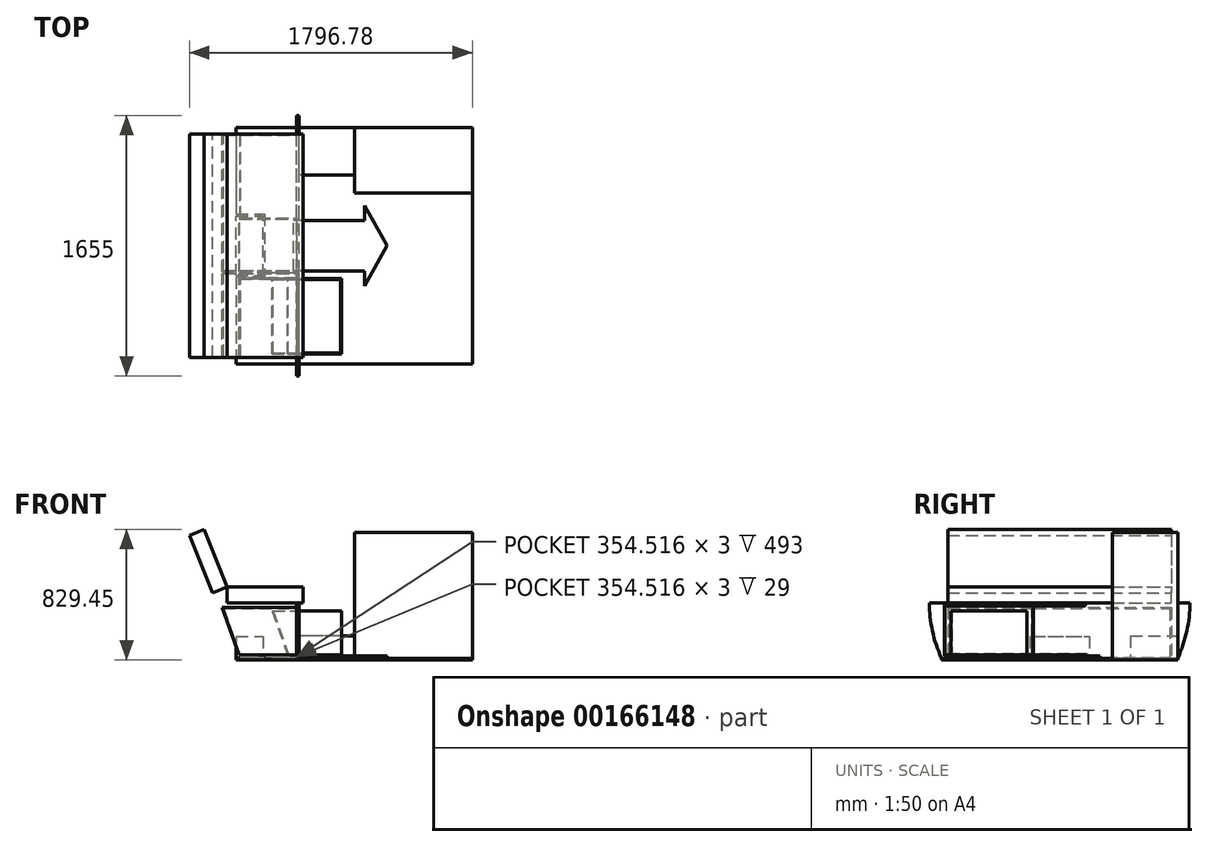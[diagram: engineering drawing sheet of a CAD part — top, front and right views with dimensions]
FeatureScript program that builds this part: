
annotation { "Feature Type Name" : "Feature", "Feature Type Description" : "" }
export const myFeature = defineFeature(function(context is Context, id is Id, definition is map)
    precondition{}
    {
        {
            var Q0;
            Q0=qCreatedBy(makeId("Top.planeOp"),FACE);
            var sketch = newSketch(context, id + "F0", { "sketchPlane" : qUnion([Q0])});
            skLineSegment(sketch, "E0.bottom", {"start": v(750, 750) * mm, "end": v(-750, 750) * mm});
            skLineSegment(sketch, "E0.top", {"start": v(750, -750) * mm, "end": v(-750, -750) * mm});
            skLineSegment(sketch, "E0.left", {"start": v(750, 750) * mm, "end": v(750, -750) * mm});
            skLineSegment(sketch, "E0.right", {"start": v(-750, 750) * mm, "end": v(-750, 200) * mm});
            skPoint(sketch, "E0.middle", {"position": v(0, 0) * mm});
            skLineSegment(sketch, "E1", {"start": v(-750, 200) * mm, "end": v(-570, 200) * mm});
            skLineSegment(sketch, "E2", {"start": v(-570, 200) * mm, "end": v(-570, -200) * mm});
            skLineSegment(sketch, "E3", {"start": v(-570, -200) * mm, "end": v(-750, -200) * mm});
            skLineSegment(sketch, "E4.trimOffspring", {"start": v(-750, -200) * mm, "end": v(-750, -750) * mm});
            skLineSegment(sketch, "E5", {"start": v(-750, 0) * mm, "end": v(750, 0) * mm, "construction": true});
            skSolve(sketch);
        }
        {
            var Q0;
            Q0=makeQuery(id+"F0.imprint","IMPRINT",FACE,{"disambiguationData":[TD([[makeQuery(id+"F0.imprint","IMPRINT",EDGE,{"derivedFrom":sQuery(id+"F0.wireOp",EDGE,"E0.bottom")}),1.0]])]});
            extrude(context, id + "F1", {"entities" : qUnion([Q0]), "depth" : 12 * mm});
        }
        {
            var Q0;
            Q0=makeQuery(id+"F1.opExtrude","CAP_FACE",FACE,{"disambiguationData":[OSD([sQuery(id+"F0.wireOp",EDGE,"E0.bottom"),sQuery(id+"F0.wireOp",EDGE,"E0.top"),sQuery(id+"F0.wireOp",EDGE,"E0.left"),sQuery(id+"F0.wireOp",EDGE,"E0.right"),sQuery(id+"F0.wireOp",EDGE,"E1"),sQuery(id+"F0.wireOp",EDGE,"E2"),sQuery(id+"F0.wireOp",EDGE,"E3"),sQuery(id+"F0.wireOp",EDGE,"E4.trimOffspring")])],"isStart":false});
            var sketch = newSketch(context, id + "F2", { "sketchPlane" : qUnion([Q0])});
            skLineSegment(sketch, "E6", {"start": v(-350, 750) * mm, "end": v(-350, -750) * mm, "construction": true});
            skLineSegment(sketch, "E7", {"start": v(0, 750) * mm, "end": v(0, 335) * mm, "construction": true});
            skLineSegment(sketch, "E8", {"start": v(0, 335) * mm, "end": v(750, 335) * mm, "construction": true});
            skLineSegment(sketch, "E9", {"start": v(-350, 450) * mm, "end": v(0, 450) * mm, "construction": true});
            skLineSegment(sketch, "E10", {"start": v(-366, 750) * mm, "end": v(-366, -750) * mm});
            skLineSegment(sketch, "E11", {"start": v(16, 466) * mm, "end": v(-366, 466) * mm});
            skLineSegment(sketch, "E12", {"start": v(16, 466) * mm, "end": v(16, 351) * mm});
            skLineSegment(sketch, "E13", {"start": v(750, 351) * mm, "end": v(16, 351) * mm});
            skLineSegment(sketch, "E14", {"start": v(-350, -750) * mm, "end": v(-350, -770) * mm});
            skLineSegment(sketch, "E15", {"start": v(-350, -770) * mm, "end": v(750, -770) * mm});
            skLineSegment(sketch, "E16", {"start": v(750, -770) * mm, "end": v(750, -750) * mm});
            skLineSegment(sketch, "E17.bottom", {"start": v(-350, -705) * mm, "end": v(750, -705) * mm});
            skLineSegment(sketch, "E17.top", {"start": v(-350, -670) * mm, "end": v(750, -670) * mm});
            skLineSegment(sketch, "E17.left", {"start": v(-350, -705) * mm, "end": v(-350, -670) * mm});
            skLineSegment(sketch, "E17.right", {"start": v(750, -705) * mm, "end": v(750, -670) * mm});
            skLineSegment(sketch, "E18", {"start": v(-350, -710) * mm, "end": v(750, -710) * mm});
            skLineSegment(sketch, "E19", {"start": v(750, -710) * mm, "end": v(750, -750) * mm});
            skLineSegment(sketch, "E20", {"start": v(-350, -710) * mm, "end": v(-350, -750) * mm});
            skLineSegment(sketch, "E21.bottom", {"start": v(-350, 450) * mm, "end": v(0, 450) * mm});
            skLineSegment(sketch, "E21.top", {"start": v(-350, 415) * mm, "end": v(0, 415) * mm});
            skLineSegment(sketch, "E21.left", {"start": v(-350, 450) * mm, "end": v(-350, 415) * mm});
            skLineSegment(sketch, "E21.right", {"start": v(0, 450) * mm, "end": v(0, 415) * mm});
            skLineSegment(sketch, "E22.bottom", {"start": v(-350, 410) * mm, "end": v(0, 410) * mm});
            skLineSegment(sketch, "E22.top", {"start": v(-350, 375) * mm, "end": v(0, 375) * mm});
            skLineSegment(sketch, "E22.left", {"start": v(-350, 410) * mm, "end": v(-350, 375) * mm});
            skLineSegment(sketch, "E22.right", {"start": v(0, 410) * mm, "end": v(0, 375) * mm});
            skLineSegment(sketch, "E23.bottom", {"start": v(-350, 370) * mm, "end": v(0, 370) * mm});
            skLineSegment(sketch, "E23.top", {"start": v(-350, 335) * mm, "end": v(0, 335) * mm});
            skLineSegment(sketch, "E23.left", {"start": v(-350, 370) * mm, "end": v(-350, 335) * mm});
            skLineSegment(sketch, "E23.right", {"start": v(0, 370) * mm, "end": v(0, 335) * mm});
            skLineSegment(sketch, "E24", {"start": v(-350, 450) * mm, "end": v(-350, -705) * mm});
            skLineSegment(sketch, "E25", {"start": v(0, 450) * mm, "end": v(0, 335) * mm});
            skLineSegment(sketch, "E26", {"start": v(0, 335) * mm, "end": v(750, 335) * mm});
            skSolve(sketch);
        }
        {
            var Q0;
            Q0=makeQuery(id+"F1.opExtrude","CAP_FACE",FACE,{"disambiguationData":[OSD([sQuery(id+"F0.wireOp",EDGE,"E0.bottom"),sQuery(id+"F0.wireOp",EDGE,"E0.top"),sQuery(id+"F0.wireOp",EDGE,"E0.left"),sQuery(id+"F0.wireOp",EDGE,"E0.right"),sQuery(id+"F0.wireOp",EDGE,"E1"),sQuery(id+"F0.wireOp",EDGE,"E2"),sQuery(id+"F0.wireOp",EDGE,"E3"),sQuery(id+"F0.wireOp",EDGE,"E4.trimOffspring")])],"isStart":false});
            var sketch = newSketch(context, id + "F3", { "sketchPlane" : qUnion([Q0])});
            skLineSegment(sketch, "E27.bottom", {"start": v(750, 750) * mm, "end": v(0, 750) * mm});
            skLineSegment(sketch, "E27.top", {"start": v(750, 335) * mm, "end": v(0, 335) * mm});
            skLineSegment(sketch, "E27.left", {"start": v(750, 750) * mm, "end": v(750, 335) * mm});
            skLineSegment(sketch, "E27.right", {"start": v(0, 750) * mm, "end": v(0, 335) * mm});
            skLineSegment(sketch, "E28", {"start": v(0, 450) * mm, "end": v(-350, 450) * mm});
            skLineSegment(sketch, "E29", {"start": v(-350, 450) * mm, "end": v(-350, 750) * mm});
            skSolve(sketch);
        }
        {
            var Q0;
            Q0=sQuery(id+"F3.wireOp",EDGE,"E28");
            var Q1;
            Q1=sQuery(id+"F3.wireOp",VERTEX,"E28.end");
            cPlane(context, id + "F4", {"entities" : qUnion([Q0, Q1]), "cplaneType" : CPlaneType.LINE_POINT, "offset" : 25 * mm, "width" : 150 * mm, "height" : 150 * mm});
        }
        {
            var Q0;
            Q0=qCreatedBy(id+"F4.planeOp",FACE);
            var sketch = newSketch(context, id + "F5", { "sketchPlane" : qUnion([Q0])});
            skLineSegment(sketch, "E30", {"start": v(827.5, 364) * mm, "end": v(-827.5, 364) * mm});
            skArc(sketch, "E31", {"start": v(750, 12) * mm, "mid": v(807.9, 183.78) * mm, "end": v(827.5, 364) * mm});
            skLineSegment(sketch, "E32", {"start": v(827.5, 72.78) * mm, "end": v(827.5, 364) * mm, "construction": true});
            skArc(sketch, "E33.MirrorCS", {"start": v(-750, 12) * mm, "mid": v(-807.9, 183.78) * mm, "end": v(-827.5, 364) * mm});
            skLineSegment(sketch, "E34", {"start": v(750, 12) * mm, "end": v(-750, 12) * mm});
            skSolve(sketch);
        }
        {
            var Q0;
            Q0=makeQuery(id+"F5.imprint","IMPRINT",FACE,{"disambiguationData":[TD([[makeQuery(id+"F5.imprint","IMPRINT",EDGE,{"derivedFrom":sQuery(id+"F5.wireOp",EDGE,"E30")}),1.0]])]});
            extrude(context, id + "F6", {"entities" : qUnion([Q0]), "operationType" : NewBodyOperationType.ADD, "depth" : 18 * mm});
        }
        {
            var Q0;
            {var subQ1=sQuery(id+"F3.wireOp",EDGE,"E27.bottom");Q0=makeQuery(id+"F3.imprint","IMPRINT",FACE,{"disambiguationData":[TD([[makeQuery(id+"F3.imprint","IMPRINT",EDGE,{"derivedFrom":subQ1}),1.0]])]});}
            extrude(context, id + "F7", {"entities" : qUnion([Q0]), "operationType" : NewBodyOperationType.ADD, "depth" : 800 * mm});
        }
        {
            var Q0;
            {var subQ3=sQuery(id+"F3.wireOp",EDGE,"E28");Q0=makeQuery(id+"F3.imprint","IMPRINT",FACE,{"disambiguationData":[TD([[makeQuery(id+"F3.imprint","IMPRINT",EDGE,{"derivedFrom":subQ3}),-1.0]])]});}
            extrude(context, id + "F8", {"entities" : qUnion([Q0]), "operationType" : NewBodyOperationType.ADD, "depth" : 140 * mm});
        }
        {
            var Q0;
            Q0=qCreatedBy(makeId("Front.planeOp"),FACE);
            var sketch = newSketch(context, id + "F9", { "sketchPlane" : qUnion([Q0])});
            skLineSegment(sketch, "E35.bottom", {"start": v(-324.6, 364) * mm, "end": v(-808.33, 364) * mm});
            skLineSegment(sketch, "E35.top", {"start": v(-324.6, 464) * mm, "end": v(-808.33, 464) * mm});
            skLineSegment(sketch, "E35.left", {"start": v(-324.6, 364) * mm, "end": v(-324.6, 464) * mm});
            skLineSegment(sketch, "E35.right", {"start": v(-808.33, 364) * mm, "end": v(-808.33, 464) * mm});
            skLineSegment(sketch, "E36", {"start": v(-839.36, 333.23) * mm, "end": v(-725.7, 12) * mm});
            skLineSegment(sketch, "E37", {"start": v(-725.7, 12) * mm, "end": v(-368, 12) * mm});
            skLineSegment(sketch, "E38", {"start": v(-368, 12) * mm, "end": v(-368, 364) * mm});
            skLineSegment(sketch, "E39.bottom", {"start": v(-953.88, 829.45) * mm, "end": v(-808.33, 464) * mm});
            skLineSegment(sketch, "E39.top", {"start": v(-1046.78, 792.45) * mm, "end": v(-901.23, 427) * mm});
            skLineSegment(sketch, "E39.left", {"start": v(-953.88, 829.45) * mm, "end": v(-1046.78, 792.45) * mm});
            skLineSegment(sketch, "E39.right", {"start": v(-808.33, 464) * mm, "end": v(-901.23, 427) * mm});
            skLineSegment(sketch, "E40", {"start": v(-839.36, 333.23) * mm, "end": v(-368, 333.23) * mm});
            skSolve(sketch);
        }
        {
            var Q0;
            Q0=makeQuery(id+"F9.imprint","IMPRINT",FACE,{"disambiguationData":[TD([[makeQuery(id+"F9.imprint","IMPRINT",EDGE,{"derivedFrom":sQuery(id+"F9.wireOp",EDGE,"E39.bottom")}),-1.0]])]});
            var Q1;
            Q1=makeQuery(id+"F9.imprint","IMPRINT",FACE,{"disambiguationData":[TD([[makeQuery(id+"F9.imprint","IMPRINT",EDGE,{"derivedFrom":sQuery(id+"F9.wireOp",EDGE,"E35.top")}),1.0]])]});
            var Q2;
            Q2=makeQuery(id+"F9.imprint","IMPRINT",FACE,{"disambiguationData":[TD([[makeQuery(id+"F9.imprint","IMPRINT",EDGE,{"derivedFrom":sQuery(id+"F9.wireOp",EDGE,"E36")}),1.0]])]});
            extrude(context, id + "F10", {"entities" : qUnion([Q0, Q1, Q2]), "endBound" : BoundingType.SYMMETRIC, "depth" : 1420 * mm, "offsetDistance" : 25 * mm});
        }
        {
            var Q0;
            Q0=makeQuery(id+"F6.opExtrude","CAP_FACE",FACE,{"disambiguationData":[OSD([sQuery(id+"F5.wireOp",EDGE,"E30"),sQuery(id+"F5.wireOp",EDGE,"E31"),sQuery(id+"F5.wireOp",EDGE,"E33.MirrorCS"),sQuery(id+"F5.wireOp",EDGE,"E34")])],"isStart":true});
            var sketch = newSketch(context, id + "F11", { "sketchPlane" : qUnion([Q0])});
            skLineSegment(sketch, "E41.bottom", {"start": v(-170, 12) * mm, "end": v(170, 12) * mm});
            skLineSegment(sketch, "E41.top", {"start": v(-170, 32) * mm, "end": v(170, 32) * mm});
            skLineSegment(sketch, "E41.left", {"start": v(-170, 12) * mm, "end": v(-170, 32) * mm});
            skLineSegment(sketch, "E41.right", {"start": v(170, 12) * mm, "end": v(170, 32) * mm});
            skLineSegment(sketch, "E42.bottom", {"start": v(-727.5, 344) * mm, "end": v(-170, 344) * mm});
            skLineSegment(sketch, "E42.top", {"start": v(-727.5, 32) * mm, "end": v(-170, 32) * mm});
            skLineSegment(sketch, "E42.left", {"start": v(-727.5, 344) * mm, "end": v(-727.5, 32) * mm});
            skLineSegment(sketch, "E42.right", {"start": v(-170, 344) * mm, "end": v(-170, 32) * mm});
            skLineSegment(sketch, "E43.bottom", {"start": v(-165, 344) * mm, "end": v(165, 344) * mm});
            skLineSegment(sketch, "E43.top", {"start": v(-165, 32) * mm, "end": v(165, 32) * mm});
            skLineSegment(sketch, "E43.left", {"start": v(-165, 344) * mm, "end": v(-165, 32) * mm});
            skLineSegment(sketch, "E43.right", {"start": v(165, 344) * mm, "end": v(165, 32) * mm});
            skPoint(sketch, "E44", {"position": v(-448.75, 32) * mm});
            skLineSegment(sketch, "E45.0", {"start": v(-732.5, 27) * mm, "end": v(-170, 27) * mm});
            skLineSegment(sketch, "E45.1", {"start": v(-732.5, 349) * mm, "end": v(-732.5, 27) * mm});
            skLineSegment(sketch, "E45.2", {"start": v(-732.5, 349) * mm, "end": v(-170, 349) * mm});
            skLineSegment(sketch, "E46", {"start": v(-170, 349) * mm, "end": v(-170, 364) * mm});
            skLineSegment(sketch, "E47", {"start": v(-165, 364) * mm, "end": v(-165, 349) * mm});
            skLineSegment(sketch, "E48", {"start": v(-165, 349) * mm, "end": v(165, 349) * mm});
            skLineSegment(sketch, "E49", {"start": v(165, 349) * mm, "end": v(165, 364) * mm});
            skLineSegment(sketch, "E50", {"start": v(165, 349) * mm, "end": v(165, 344) * mm});
            skPoint(sketch, "E51", {"position": v(-689, 32) * mm});
            skLineSegment(sketch, "E52", {"start": v(-448.75, 32) * mm, "end": v(-448.75, 56.15) * mm, "construction": true});
            skPoint(sketch, "E53.MirrorP", {"position": v(-208.5, 32) * mm});
            skSolve(sketch);
        }
        {
            var Q0;
            Q0=makeQuery(id+"F11.imprint","IMPRINT",FACE,{"disambiguationData":[TD([[makeQuery(id+"F11.imprint","IMPRINT",EDGE,{"derivedFrom":sQuery(id+"F11.wireOp",EDGE,"E41.bottom")}),1.0]])]});
            var Q1;
            Q1=makeQuery(id+"F11.imprint","IMPRINT",FACE,{"disambiguationData":[TD([[makeQuery(id+"F11.imprint","IMPRINT",EDGE,{"derivedFrom":sQuery(id+"F11.wireOp",EDGE,"E42.bottom")}),1.0]])]});
            extrude(context, id + "F12", {"entities" : qUnion([Q0, Q1]), "operationType" : NewBodyOperationType.REMOVE, "endBound" : BoundingType.THROUGH_ALL, "oppositeDirection" : true, "depth" : 25 * mm, "offsetDistance" : 25 * mm});
        }
        {
            var Q0;
            Q0=makeQuery(id+"F10.opExtrude","SWEPT_FACE",FACE,{"disambiguationData":[OSD([sQuery(id+"F9.wireOp",EDGE,"E38")])]});
            shell(context, id + "F13", {"entities" : qUnion([Q0]), "thickness" : 6 * mm});
        }
        {
            var Q0;
            Q0=makeQuery(id+"F10.opExtrude","SWEPT_FACE",FACE,{"disambiguationData":[OSD([sQuery(id+"F9.wireOp",EDGE,"E38")])]});
            var sketch = newSketch(context, id + "F14", { "sketchPlane" : qUnion([Q0])});
            skLineSegment(sketch, "E54", {"start": v(-205, 327.23) * mm, "end": v(-205, 18) * mm});
            skLineSegment(sketch, "E55", {"start": v(-211, 327.23) * mm, "end": v(-211, 18) * mm});
            skLineSegment(sketch, "E56.MirrorCS", {"start": v(205, 327.23) * mm, "end": v(205, 18) * mm});
            skLineSegment(sketch, "E57.MirrorCS", {"start": v(211, 327.23) * mm, "end": v(211, 18) * mm});
            skLineSegment(sketch, "E58", {"start": v(704, 146) * mm, "end": v(456, 146) * mm});
            skLineSegment(sketch, "E59", {"start": v(456, 146) * mm, "end": v(456, 18) * mm});
            skLineSegment(sketch, "E60.0", {"start": v(450, 152) * mm, "end": v(450, 18) * mm});
            skLineSegment(sketch, "E60.1", {"start": v(704, 152) * mm, "end": v(450, 152) * mm});
            skSolve(sketch);
        }
        {
            var Q0;
            {var subQ0=sQuery(id+"F14.wireOp",EDGE,"E54");Q0=makeQuery(id+"F14.imprint","IMPRINT",FACE,{"disambiguationData":[TD([[makeQuery(id+"F14.imprint","IMPRINT",EDGE,{"derivedFrom":subQ0}),-1.0]])]});}
            var Q1;
            {var subQ0=sQuery(id+"F14.wireOp",EDGE,"E56.MirrorCS");Q1=makeQuery(id+"F14.imprint","IMPRINT",FACE,{"disambiguationData":[TD([[makeQuery(id+"F14.imprint","IMPRINT",EDGE,{"derivedFrom":subQ0}),1.0]])]});}
            var Q2;
            {var subQ3=sQuery(id+"F14.wireOp",EDGE,"E58");Q2=makeQuery(id+"F14.imprint","IMPRINT",FACE,{"disambiguationData":[TD([[makeQuery(id+"F14.imprint","IMPRINT",EDGE,{"derivedFrom":subQ3}),-1.0]])]});}
            var Q3;
            Q3=makeQuery(id+"F13.opShell","OFFSET_FACE",FACE,{"disambiguationData":[OSD([sQuery(id+"F9.wireOp",EDGE,"E36")])]});
            extrude(context, id + "F15", {"entities" : qUnion([Q0, Q1, Q2]), "operationType" : NewBodyOperationType.ADD, "endBound" : BoundingType.UP_TO_SURFACE, "oppositeDirection" : true, "depth" : 25 * mm, "endBoundEntityFace" : qUnion([Q3]), "offsetDistance" : 25 * mm});
        }
        {
            var Q0;
            Q0=sQuery(id+"F11.wireOp",EDGE,"E42.top");
            cPoint(context, id + "F16", {"entities" : qUnion([Q0]), "parameter" : 0.5});
        }
        {
            var Q0;
            Q0 = qCreatedBy(id + "F16" ,VERTEX);
            var Q1;
            Q1=qCreatedBy(makeId("Front.planeOp"),FACE);
            cPlane(context, id + "F17", {"entities" : qUnion([Q0, Q1]), "cplaneType" : CPlaneType.PLANE_POINT, "offset" : 25 * mm, "width" : 150 * mm, "height" : 150 * mm});
        }
        {
            var Q0;
            Q0=qCreatedBy(id+"F17.planeOp",FACE);
            var sketch = newSketch(context, id + "F18", { "sketchPlane" : qUnion([Q0])});
            skLineSegment(sketch, "E61.0", {"start": v(-809.65, 312.23) * mm, "end": v(-368, 312.23) * mm});
            skLineSegment(sketch, "E61.1", {"start": v(-809.65, 312.23) * mm, "end": v(-710.85, 33) * mm});
            skLineSegment(sketch, "E61.2", {"start": v(-710.85, 33) * mm, "end": v(-368, 33) * mm});
            skLineSegment(sketch, "E62", {"start": v(-368, 312.23) * mm, "end": v(-368, 33) * mm});
            skSolve(sketch);
        }
        {
            var Q0;
            Q0=makeQuery(id+"F18.imprint","IMPRINT",FACE,{"disambiguationData":[TD([[makeQuery(id+"F18.imprint","IMPRINT",EDGE,{"derivedFrom":sQuery(id+"F18.wireOp",EDGE,"E61.0")}),-1.0]])]});
            var Q1;
            Q1=sQuery(id+"F11.wireOp",VERTEX,"E51");
            var Q2;
            Q2=sQuery(id+"F11.wireOp",VERTEX,"E53.MirrorP");
            extrude(context, id + "F19", {"entities" : qUnion([Q0]), "endBound" : BoundingType.UP_TO_VERTEX, "depth" : 25 * mm, "endBoundEntityVertex" : qUnion([Q1]), "offsetDistance" : 25 * mm, "hasSecondDirection" : true, "secondDirectionBound" : SecondDirectionBoundingType.UP_TO_VERTEX, "secondDirectionOppositeDirection" : true, "secondDirectionDepth" : 25 * mm, "secondDirectionBoundEntityVertex" : qUnion([Q2])});
        }
        {
            var Q0;
            Q0=makeQuery(id+"F19.opExtrude","SWEPT_FACE",FACE,{"disambiguationData":[OSD([sQuery(id+"F18.wireOp",EDGE,"E61.0")])]});
            shell(context, id + "F20", {"entities" : qUnion([Q0]), "thickness" : 6 * mm});
        }
        {
            var Q0;
            Q0=makeQuery(id+"F1.opExtrude","CAP_FACE",FACE,{"disambiguationData":[OSD([sQuery(id+"F0.wireOp",EDGE,"E0.bottom"),sQuery(id+"F0.wireOp",EDGE,"E0.top"),sQuery(id+"F0.wireOp",EDGE,"E0.left"),sQuery(id+"F0.wireOp",EDGE,"E0.right"),sQuery(id+"F0.wireOp",EDGE,"E1"),sQuery(id+"F0.wireOp",EDGE,"E2"),sQuery(id+"F0.wireOp",EDGE,"E3"),sQuery(id+"F0.wireOp",EDGE,"E4.trimOffspring")])],"isStart":true});
            var sketch = newSketch(context, id + "F21", { "sketchPlane" : qUnion([Q0])});
            skLineSegment(sketch, "E63.bottom", {"start": v(-750, 190) * mm, "end": v(-580, 190) * mm});
            skLineSegment(sketch, "E63.top", {"start": v(-750, -190) * mm, "end": v(-580, -190) * mm});
            skLineSegment(sketch, "E63.left", {"start": v(-750, 190) * mm, "end": v(-750, -190) * mm});
            skLineSegment(sketch, "E63.right", {"start": v(-580, 190) * mm, "end": v(-580, -190) * mm});
            skSolve(sketch);
        }
        {
            var Q0;
            Q0=makeQuery(id+"F21.imprint","IMPRINT",FACE,{"disambiguationData":[TD([[makeQuery(id+"F21.imprint","IMPRINT",EDGE,{"derivedFrom":sQuery(id+"F21.wireOp",EDGE,"E63.bottom")}),-1.0]])]});
            extrude(context, id + "F22", {"entities" : qUnion([Q0]), "oppositeDirection" : true, "depth" : 150 * mm, "offsetDistance" : 25 * mm});
        }
        {
            var Q0;
            {var subQ3=sQuery(id+"F3.wireOp",EDGE,"E27.top");Q0=makeQuery(id+"F3.imprint","IMPRINT",FACE,{"disambiguationData":[TD([[makeQuery(id+"F3.imprint","IMPRINT",EDGE,{"derivedFrom":subQ3}),1.0]])]});}
            var sketch = newSketch(context, id + "F23", { "sketchPlane" : qUnion([Q0])});
            skLineSegment(sketch, "E64.bottom", {"start": v(65, -160) * mm, "end": v(-385, -160) * mm});
            skLineSegment(sketch, "E64.top", {"start": v(65, 160) * mm, "end": v(-385, 160) * mm});
            skLineSegment(sketch, "E64.left", {"start": v(65, -160) * mm, "end": v(65, 160) * mm});
            skLineSegment(sketch, "E64.right", {"start": v(-385, -160) * mm, "end": v(-385, 160) * mm});
            skPoint(sketch, "E64.middle", {"position": v(-160, 0) * mm});
            skLineSegment(sketch, "E65", {"start": v(65, 160) * mm, "end": v(65, 255.4) * mm});
            skLineSegment(sketch, "E66", {"start": v(65, 255.4) * mm, "end": v(209.1, 0) * mm});
            skLineSegment(sketch, "E67.MirrorCS", {"start": v(65, -255.4) * mm, "end": v(209.1, 0) * mm});
            skLineSegment(sketch, "E68.MirrorCS", {"start": v(65, -160) * mm, "end": v(65, -255.4) * mm});
            skSolve(sketch);
        }
        {
            var Q0;
            Q0 = qSketchRegion(id + "F23", true);
            extrude(context, id + "F24", {"entities" : qUnion([Q0]), "depth" : 15 * mm, "offsetDistance" : 25 * mm, "hasSecondDirection" : true, "secondDirectionOppositeDirection" : false, "secondDirectionDepth" : 10 * mm});
        }
        {
            var Q0;
            Q0=makeQuery(id+"F19.opExtrude","SWEPT_BODY",BODY,{"disambiguationData":[OSD([sQuery(id+"F18.wireOp",EDGE,"E61.0"),sQuery(id+"F18.wireOp",EDGE,"E61.1"),sQuery(id+"F18.wireOp",EDGE,"E61.2"),sQuery(id+"F18.wireOp",EDGE,"E62")])]});
            transform(context, id + "F25", {"entities" : qUnion([Q0]), "transformType" : TransformType.TRANSLATION_3D, "dx" : 287 * mm, "dy" : 0 * mm, "dz" : 0 * mm, "makeCopy" : false});
        }
    });
